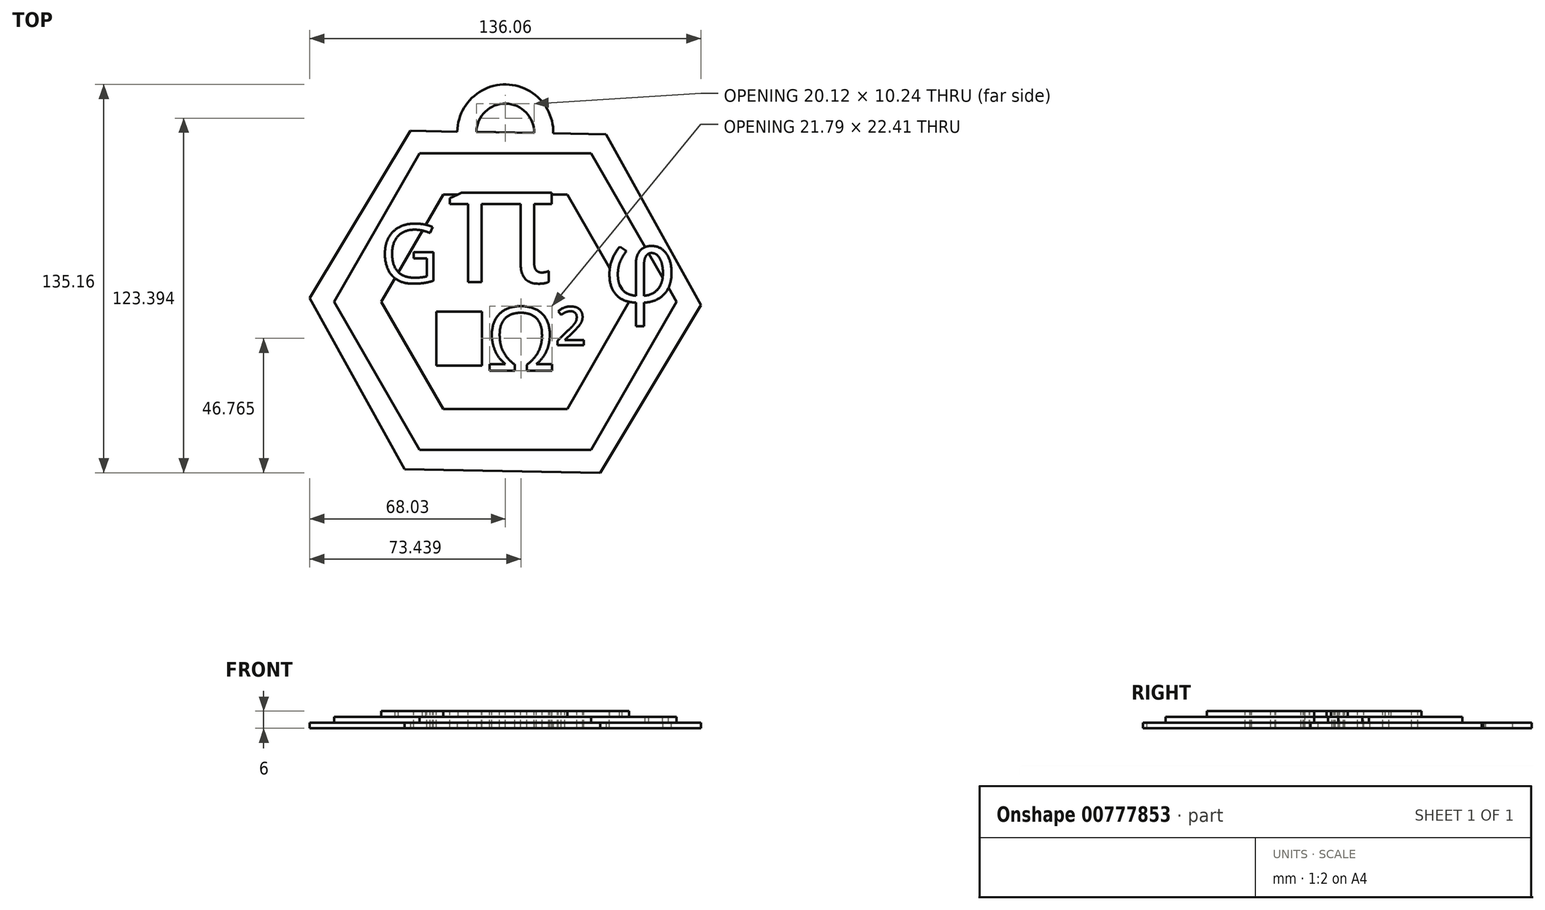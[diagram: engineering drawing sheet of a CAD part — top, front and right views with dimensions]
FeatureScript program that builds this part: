
annotation { "Feature Type Name" : "Feature", "Feature Type Description" : "" }
export const myFeature = defineFeature(function(context is Context, id is Id, definition is map)
    precondition{}
    {
        {
            var Q0;
            Q0=qCreatedBy(makeId("Top.planeOp"),FACE);
            var sketch = newSketch(context, id + "F0", { "sketchPlane" : qUnion([Q0])});
            skCircle(sketch, "E0.cCircle", {"center": v(0, 0) * mm, "radius": 58.93 * mm, "construction": true});
            skLineSegment(sketch, "E0.0", {"start": v(68.03, -1.22) * mm, "end": v(32.96, -59.52) * mm});
            skLineSegment(sketch, "E0.1", {"start": v(32.96, -59.52) * mm, "end": v(-35.07, -58.3) * mm});
            skLineSegment(sketch, "E0.2", {"start": v(-35.07, -58.3) * mm, "end": v(-68.03, 1.22) * mm});
            skLineSegment(sketch, "E0.3", {"start": v(-68.03, 1.22) * mm, "end": v(-32.96, 59.52) * mm});
            skLineSegment(sketch, "E0.4", {"start": v(-32.96, 59.52) * mm, "end": v(35.07, 58.3) * mm});
            skLineSegment(sketch, "E0.5", {"start": v(35.07, 58.3) * mm, "end": v(68.03, -1.22) * mm});
            skPoint(sketch, "E0.0.midPoint", {"position": v(50.5, -30.37) * mm});
            skSolve(sketch);
        }
        {
            var Q0;
            Q0=makeQuery(id+"F0.imprint","IMPRINT",FACE,{"disambiguationData":[TD([[makeQuery(id+"F0.imprint","IMPRINT",EDGE,{"derivedFrom":sQuery(id+"F0.wireOp",EDGE,"E0.0")}),-1.0]])]});
            extrude(context, id + "F1", {"entities" : qUnion([Q0]), "depth" : 2 * mm, "offsetDistance" : 25.4 * mm});
        }
        {
            var Q0;
            Q0=makeQuery(id+"F1.opExtrude","CAP_FACE",FACE,{"disambiguationData":[OSD([sQuery(id+"F0.wireOp",EDGE,"E0.0"),sQuery(id+"F0.wireOp",EDGE,"E0.1"),sQuery(id+"F0.wireOp",EDGE,"E0.2"),sQuery(id+"F0.wireOp",EDGE,"E0.3"),sQuery(id+"F0.wireOp",EDGE,"E0.4"),sQuery(id+"F0.wireOp",EDGE,"E0.5")])],"isStart":false});
            var sketch = newSketch(context, id + "F2", { "sketchPlane" : qUnion([Q0])});
            skSolve(sketch);
        }
        {
            var Q0;
            Q0=makeQuery(id+"F2.imprint","IMPRINT",FACE,{"disambiguationData":[TD([[makeQuery(id+"F2.imprint","IMPRINT",EDGE,{"derivedFrom":makeQuery(id+"F1.opExtrude","CAP_EDGE",EDGE,{"disambiguationData":[OSD([sQuery(id+"F0.wireOp",EDGE,"E0.0")])],"isStart":false})}),-1.0]])]});
            var sketch = newSketch(context, id + "F3", { "sketchPlane" : qUnion([Q0])});
            skCircle(sketch, "E1.cCircle", {"center": v(0, 0) * mm, "radius": 51.63 * mm, "construction": true});
            skLineSegment(sketch, "E1.0", {"start": v(-29.8, 51.63) * mm, "end": v(29.8, 51.63) * mm});
            skLineSegment(sketch, "E1.1", {"start": v(29.8, 51.63) * mm, "end": v(59.61, 0) * mm});
            skLineSegment(sketch, "E1.2", {"start": v(59.61, 0) * mm, "end": v(29.8, -51.63) * mm});
            skLineSegment(sketch, "E1.3", {"start": v(29.8, -51.63) * mm, "end": v(-29.8, -51.63) * mm});
            skLineSegment(sketch, "E1.4", {"start": v(-29.8, -51.63) * mm, "end": v(-59.61, 0) * mm});
            skLineSegment(sketch, "E1.5", {"start": v(-59.61, 0) * mm, "end": v(-29.8, 51.63) * mm});
            skPoint(sketch, "E1.0.midPoint", {"position": v(0, 51.63) * mm});
            skSolve(sketch);
        }
        {
            var Q0;
            Q0=makeQuery(id+"F3.imprint","IMPRINT",FACE,{"disambiguationData":[TD([[makeQuery(id+"F3.imprint","IMPRINT",EDGE,{"derivedFrom":sQuery(id+"F3.wireOp",EDGE,"E1.0")}),-1.0]])]});
            extrude(context, id + "F4", {"entities" : qUnion([Q0]), "operationType" : NewBodyOperationType.ADD, "depth" : 2 * mm, "offsetDistance" : 25.4 * mm});
        }
        {
            var Q0;
            Q0=makeQuery(id+"F4.opExtrude","CAP_FACE",FACE,{"disambiguationData":[OSD([sQuery(id+"F3.wireOp",EDGE,"E1.0"),sQuery(id+"F3.wireOp",EDGE,"E1.1"),sQuery(id+"F3.wireOp",EDGE,"E1.2"),sQuery(id+"F3.wireOp",EDGE,"E1.3"),sQuery(id+"F3.wireOp",EDGE,"E1.4"),sQuery(id+"F3.wireOp",EDGE,"E1.5")])],"isStart":false});
            var sketch = newSketch(context, id + "F5", { "sketchPlane" : qUnion([Q0])});
            skCircle(sketch, "E2.cCircle", {"center": v(0, 0) * mm, "radius": 37.36 * mm, "construction": true});
            skLineSegment(sketch, "E2.0", {"start": v(-21.57, 37.36) * mm, "end": v(21.57, 37.36) * mm});
            skLineSegment(sketch, "E2.1", {"start": v(21.57, 37.36) * mm, "end": v(43.14, 0) * mm});
            skLineSegment(sketch, "E2.2", {"start": v(43.14, 0) * mm, "end": v(21.57, -37.36) * mm});
            skLineSegment(sketch, "E2.3", {"start": v(21.57, -37.36) * mm, "end": v(-21.57, -37.36) * mm});
            skLineSegment(sketch, "E2.4", {"start": v(-21.57, -37.36) * mm, "end": v(-43.14, 0) * mm});
            skLineSegment(sketch, "E2.5", {"start": v(-43.14, 0) * mm, "end": v(-21.57, 37.36) * mm});
            skPoint(sketch, "E2.0.midPoint", {"position": v(0, 37.36) * mm});
            skSolve(sketch);
        }
        {
            var Q0;
            Q0=makeQuery(id+"F5.imprint","IMPRINT",FACE,{"disambiguationData":[TD([[makeQuery(id+"F5.imprint","IMPRINT",EDGE,{"derivedFrom":sQuery(id+"F5.wireOp",EDGE,"E2.0")}),-1.0]])]});
            extrude(context, id + "F6", {"entities" : qUnion([Q0]), "operationType" : NewBodyOperationType.ADD, "depth" : 2 * mm, "offsetDistance" : 25.4 * mm});
        }
        {
            var Q0;
            Q0=makeQuery(id+"F6.opExtrude","CAP_FACE",FACE,{"disambiguationData":[OSD([sQuery(id+"F5.wireOp",EDGE,"E2.0"),sQuery(id+"F5.wireOp",EDGE,"E2.1"),sQuery(id+"F5.wireOp",EDGE,"E2.2"),sQuery(id+"F5.wireOp",EDGE,"E2.3"),sQuery(id+"F5.wireOp",EDGE,"E2.4"),sQuery(id+"F5.wireOp",EDGE,"E2.5")])],"isStart":false});
            var sketch = newSketch(context, id + "F7", { "sketchPlane" : qUnion([Q0])});
            skCircle(sketch, "E3.cCircle", {"center": v(0, 0) * mm, "radius": 26.93 * mm, "construction": true});
            skLineSegment(sketch, "E3.0", {"start": v(15.55, -26.93) * mm, "end": v(-15.55, -26.93) * mm});
            skLineSegment(sketch, "E3.1", {"start": v(-15.55, -26.93) * mm, "end": v(-31.1, 0) * mm});
            skLineSegment(sketch, "E3.2", {"start": v(-31.1, 0) * mm, "end": v(-15.55, 26.93) * mm});
            skLineSegment(sketch, "E3.3", {"start": v(-15.55, 26.93) * mm, "end": v(15.55, 26.93) * mm});
            skLineSegment(sketch, "E3.4", {"start": v(15.55, 26.93) * mm, "end": v(31.1, 0) * mm});
            skLineSegment(sketch, "E3.5", {"start": v(31.1, 0) * mm, "end": v(15.55, -26.93) * mm});
            skPoint(sketch, "E3.0.midPoint", {"position": v(0, -26.93) * mm});
            skSolve(sketch);
        }
        {
            var Q0;
            Q0=makeQuery(id+"F1.opExtrude","CAP_FACE",FACE,{"disambiguationData":[OSD([sQuery(id+"F0.wireOp",EDGE,"E0.0"),sQuery(id+"F0.wireOp",EDGE,"E0.1"),sQuery(id+"F0.wireOp",EDGE,"E0.2"),sQuery(id+"F0.wireOp",EDGE,"E0.3"),sQuery(id+"F0.wireOp",EDGE,"E0.4"),sQuery(id+"F0.wireOp",EDGE,"E0.5")])],"isStart":true});
            var sketch = newSketch(context, id + "F8", { "sketchPlane" : qUnion([Q0])});
            skCircle(sketch, "E4", {"center": v(0, -58.94) * mm, "radius": 16.7 * mm});
            skCircle(sketch, "E5", {"center": v(0, -58.94) * mm, "radius": 10.06 * mm});
            skSolve(sketch);
        }
        {
            var Q0;
            {var subQ0=sQuery(id+"F8.wireOp",EDGE,"E4");var subQ1=makeQuery(id+"F1.opExtrude","CAP_EDGE",EDGE,{"disambiguationData":[OSD([sQuery(id+"F0.wireOp",EDGE,"E0.4")])],"isStart":true});var subQ2=makeQuery(id+"F8.imprint","INTERSECT",VERTEX,{"disambiguationData":[OD(0.0)],"derivedFrom":[subQ1,subQ0]});Q0=makeQuery(id+"F8.imprint","IMPRINT",FACE,{"disambiguationData":[TD([[makeQuery(id+"F8.imprint","IMPRINT",EDGE,{"disambiguationData":[TD([[subQ2,-1.0]])],"derivedFrom":subQ0}),1.0]])]});}
            extrude(context, id + "F9", {"entities" : qUnion([Q0]), "operationType" : NewBodyOperationType.ADD, "oppositeDirection" : true, "depth" : 2 * mm, "offsetDistance" : 25.4 * mm});
        }
        {
            var Q0;
            Q0=makeQuery(id+"F7.imprint","IMPRINT",FACE,{"disambiguationData":[TD([[makeQuery(id+"F7.imprint","IMPRINT",EDGE,{"derivedFrom":sQuery(id+"F7.wireOp",EDGE,"E3.0")}),-1.0]])]});
            var sketch = newSketch(context, id + "F10", { "sketchPlane" : qUnion([Q0])});
            skText(sketch, "E6", { "text": "G", "fontName": "OpenSans-Regular.ttf"});
            const initialGuessF10  = {"E6": [-0.04364, 0.00656, 1, 0, 0.02054]};
            skSetInitialGuess(sketch, initialGuessF10);
            skSolve(sketch);
        }
        {
            var Q0;
            Q0 = qSketchRegion(id + "F10", true);
            extrude(context, id + "F11", {"entities" : qUnion([Q0]), "operationType" : NewBodyOperationType.REMOVE, "oppositeDirection" : true, "depth" : 25.4 * mm, "offsetDistance" : 25.4 * mm});
        }
        {
            var Q0;
            Q0=makeQuery(id+"F7.imprint","IMPRINT",FACE,{"disambiguationData":[TD([[makeQuery(id+"F7.imprint","IMPRINT",EDGE,{"derivedFrom":sQuery(id+"F7.wireOp",EDGE,"E3.0")}),-1.0]])]});
            var sketch = newSketch(context, id + "F12", { "sketchPlane" : qUnion([Q0])});
            skText(sketch, "E7", { "text": "π", "fontName": "OpenSans-Regular.ttf"});
            const initialGuessF12  = {"E7": [-0.01997, 0.00684, 1, 0, 0.04193]};
            skSetInitialGuess(sketch, initialGuessF12);
            skSolve(sketch);
        }
        {
            var Q0;
            Q0 = qSketchRegion(id + "F12", true);
            extrude(context, id + "F13", {"entities" : qUnion([Q0]), "operationType" : NewBodyOperationType.REMOVE, "oppositeDirection" : true, "depth" : 25.4 * mm, "offsetDistance" : 25.4 * mm});
        }
        {
            var Q0;
            Q0=makeQuery(id+"F7.imprint","IMPRINT",FACE,{"disambiguationData":[TD([[makeQuery(id+"F7.imprint","IMPRINT",EDGE,{"derivedFrom":sQuery(id+"F7.wireOp",EDGE,"E3.0")}),-1.0]])]});
            var sketch = newSketch(context, id + "F14", { "sketchPlane" : qUnion([Q0])});
            skText(sketch, "E8", { "text": "↕Ω²", "fontName": "OpenSans-Regular.ttf"});
            const initialGuessF14  = {"E8": [-0.02539, -0.02396, 1, 0, 0.02225]};
            skSetInitialGuess(sketch, initialGuessF14);
            skSolve(sketch);
        }
        {
            var Q0;
            Q0 = qSketchRegion(id + "F14", true);
            extrude(context, id + "F15", {"entities" : qUnion([Q0]), "operationType" : NewBodyOperationType.REMOVE, "oppositeDirection" : true, "depth" : 25.4 * mm, "offsetDistance" : 25.4 * mm});
        }
        {
            var Q0;
            Q0=makeQuery(id+"F7.imprint","IMPRINT",FACE,{"disambiguationData":[TD([[makeQuery(id+"F7.imprint","IMPRINT",EDGE,{"derivedFrom":sQuery(id+"F7.wireOp",EDGE,"E3.0")}),1.0]])]});
            var sketch = newSketch(context, id + "F16", { "sketchPlane" : qUnion([Q0])});
            skText(sketch, "E9", { "text": "φ", "fontName": "OpenSans-Regular.ttf"});
            const initialGuessF16  = {"E9": [0.03423, 0, 1, 0, 0.02567]};
            skSetInitialGuess(sketch, initialGuessF16);
            skSolve(sketch);
        }
        {
            var Q0;
            Q0 = qSketchRegion(id + "F16", true);
            extrude(context, id + "F17", {"entities" : qUnion([Q0]), "operationType" : NewBodyOperationType.REMOVE, "oppositeDirection" : true, "depth" : 25.4 * mm, "offsetDistance" : 25.4 * mm});
        }
    });
